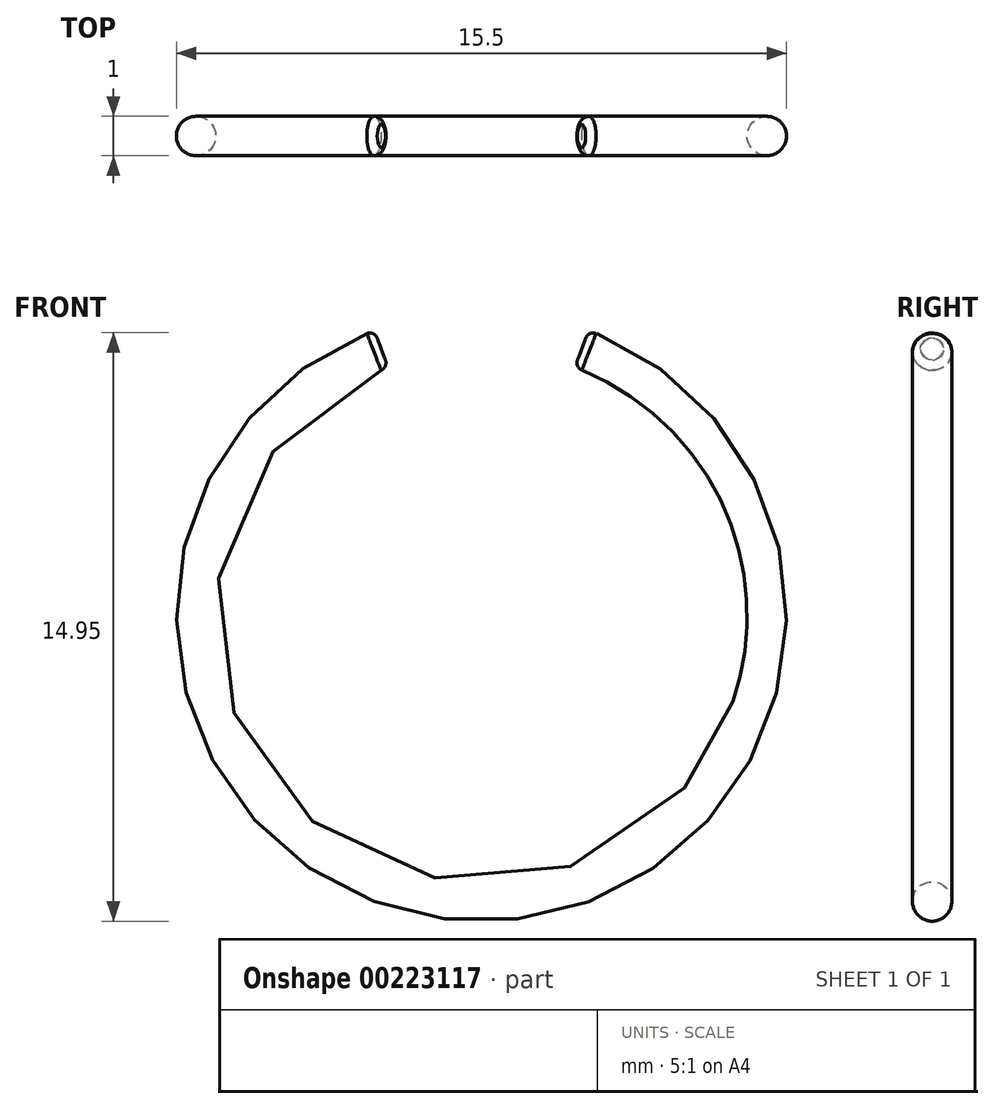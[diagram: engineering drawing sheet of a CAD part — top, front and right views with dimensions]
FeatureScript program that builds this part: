
annotation { "Feature Type Name" : "Feature", "Feature Type Description" : "" }
export const myFeature = defineFeature(function(context is Context, id is Id, definition is map)
    precondition{}
    {
        {
            var Q0;
            Q0=qCreatedBy(makeId("Front.planeOp"),FACE);
            var sketch = newSketch(context, id + "F0", { "sketchPlane" : qUnion([Q0])});
            skCircle(sketch, "E0", {"center": v(0, 0) * mm, "radius": 7.25 * mm});
            skSolve(sketch);
        }
        {
            var Q0;
            Q0=qCreatedBy(makeId("Top.planeOp"),FACE);
            var sketch = newSketch(context, id + "F1", { "sketchPlane" : qUnion([Q0])});
            skCircle(sketch, "E1", {"center": v(7.25, 0) * mm, "radius": 0.5 * mm});
            skSolve(sketch);
        }
        {
            var Q0;
            Q0=makeQuery(id+"F1.imprint","IMPRINT",FACE,{"disambiguationData":[TD([[makeQuery(id+"F1.imprint","IMPRINT",EDGE,{"derivedFrom":sQuery(id+"F1.wireOp",EDGE,"E1")}),1.0]])]});
            var Q1;
            Q1=sQuery(id+"F0.wireOp",EDGE,"E0");
            sweep(context, id + "F2", {"profiles" : qUnion([Q0]), "path" : qUnion([Q1])});
        }
        {
            var Q0;
            Q0=qCreatedBy(makeId("Front.planeOp"),FACE);
            var sketch = newSketch(context, id + "F3", { "sketchPlane" : qUnion([Q0])});
            skLineSegment(sketch, "E2", {"start": v(0, 0) * mm, "end": v(3, 8) * mm});
            skLineSegment(sketch, "E3", {"start": v(3, 8) * mm, "end": v(-3, 8) * mm});
            skLineSegment(sketch, "E4", {"start": v(-3, 8) * mm, "end": v(0, 0) * mm});
            skPoint(sketch, "E5", {"position": v(0, 8) * mm});
            skSolve(sketch);
        }
        {
            var Q0;
            Q0 = qSketchRegion(id + "F3", true);
            extrude(context, id + "F4", {"entities" : qUnion([Q0]), "operationType" : NewBodyOperationType.REMOVE, "endBound" : BoundingType.SYMMETRIC, "oppositeDirection" : true, "depth" : 25 * mm});
        }
        {
            var Q0;
            Q0=makeQuery(id+"F4.boolean.opBoolean","INTERSECT",EDGE,{"derivedFrom":[makeQuery(id+"F2.opSweep","SWEPT_FACE",FACE,{"disambiguationData":[OSD([sQuery(id+"F0.wireOp",EDGE,"E0"),sQuery(id+"F1.wireOp",EDGE,"E1")])]}),makeQuery(id+"F4.opExtrude","SWEPT_FACE",FACE,{"disambiguationData":[OSD([sQuery(id+"F3.wireOp",EDGE,"E4")])]})]});
            var Q1;
            Q1=makeQuery(id+"F4.boolean.opBoolean","INTERSECT",EDGE,{"derivedFrom":[makeQuery(id+"F2.opSweep","SWEPT_FACE",FACE,{"disambiguationData":[OSD([sQuery(id+"F0.wireOp",EDGE,"E0"),sQuery(id+"F1.wireOp",EDGE,"E1")])]}),makeQuery(id+"F4.opExtrude","SWEPT_FACE",FACE,{"disambiguationData":[OSD([sQuery(id+"F3.wireOp",EDGE,"E2")])]})]});
            fillet(context, id + "F5", {"entities" : qUnion([Q0, Q1]), "radius" : .2 * mm, "tangentPropagation" : true, "allowEdgeOverflow" : false});
        }
    });
